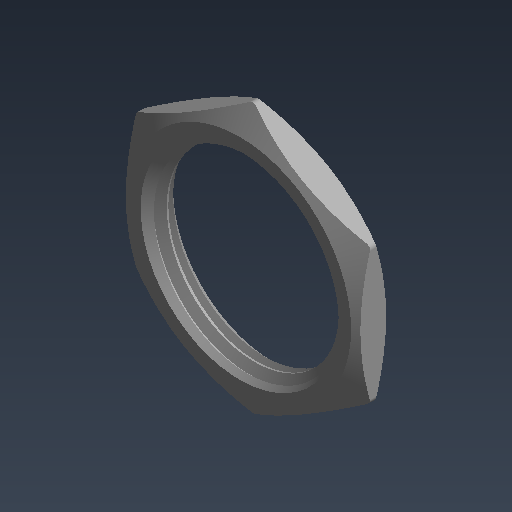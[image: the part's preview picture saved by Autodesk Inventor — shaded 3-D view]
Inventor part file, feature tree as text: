
AUTODESK INVENTOR PART (.ipt)
format: ipt  version: 2025.3 (Build 293356000, 356)  size: 204,800 bytes
history: native  units: mm (DEFAULTED — no unit token found)
features: mirror x1
ambient origin geometry x8: Origin, YZ Plane, XZ Plane, XY Plane, X Axis, Y Axis, Z Axis, Center Point
bodies: Solid1 (feature_tree)
feature tree (1):
  mirror  "Mirror1"
